FCSTD DOCUMENT  (FreeCAD 0.19R24291 (Git))
Label: battery-charger-assembly
License: All rights reserved
LicenseURL: http://en.wikipedia.org/wiki/All_rights_reserved
objects: App::Link×5, App::DocumentObjectGroup×2, PartDesign::CoordinateSystem×1, App::FeaturePython×1, App::Part×1
note: 1 computed .brp shape members not serialized (recipe doc carries the construction recipe); baked Part::Feature solids carry a one-line shape summary decoded from their .brp
EXTERNAL_REF file=battery-charger.FCStd obj=LCS_0
EXTERNAL_REF file=battery-charger.FCStd obj=battery_charger_part
EXTERNAL_REF file=micro-usb-b-connector.FCStd obj=LCS_0
EXTERNAL_REF file=micro-usb-b-connector.FCStd obj=micro_usb_b_part
EXTERNAL_REF file=usb-a-connector.FCStd obj=LCS_0
EXTERNAL_REF file=usb-a-connector.FCStd obj=usb_a_connector_part
EXTERNAL_REF file=slide_switch.FCStd obj=LCS_0
EXTERNAL_REF file=slide_switch.FCStd obj=switch_part
EXTERNAL_REF file=16340-battery.FCStd obj=LCS_0
EXTERNAL_REF file=16340-battery.FCStd obj=_6340_battery_part

FEATURE [App::DocumentObjectGroup] Parts
FEATURE [PartDesign::CoordinateSystem] LCS_Origin
  AttacherType = Attacher::AttachEngine3D
  MapMode = 2
  Support = -> [X_Axis]
FEATURE [App::DocumentObjectGroup] Constraints
FEATURE [App::FeaturePython] Variables  # WARN: FeaturePython — macro-defined, semantics opaque (R4)
FEATURE [App::Link] Unnamed_battery_charger_pcb_part  label="pcb"
  AssemblyType = Asm4EE
  AttachedBy = #LCS_0
  AttachedTo = Parent Assembly#LCS_Origin
  LinkedObject = -> <external battery-charger.FCStd>#battery_charger_part
  expr: Placement = LCS_Origin.Placement * AttachmentOffset * Unnamed#LCS_0.Placement ^ -1
FEATURE [App::Link] micro_usb
  AssemblyType = Asm4EE
  AttachedBy = #LCS_0
  AttachedTo = Unnamed_battery_charger_pcb_part#LCS_0
  AttachmentOffset = pos=(0,-27,1) rot=(0,0,1;1.5708rad)
  LinkPlacement = pos=(0,-27,1) rot=(0,0,1;1.5708rad)
  LinkedObject = -> <external micro-usb-b-connector.FCStd>#micro_usb_b_part
  Placement = pos=(0,-27,1) rot=(0,0,1;1.5708rad)
  expr: Placement = Unnamed_battery_charger_pcb_part.Placement * Unnamed#LCS_0.Placement * AttachmentOffset * Unnamed1#LCS_0.Placement ^ -1
FEATURE [App::Link] usb_a
  AssemblyType = Asm4EE
  AttachedBy = #LCS_0
  AttachedTo = Unnamed_battery_charger_pcb_part#LCS_0
  AttachmentOffset = pos=(0,30,0) rot=(0,0,1;0rad)
  LinkPlacement = pos=(0,30,0) rot=(0,0,1;0rad)
  LinkedObject = -> <external usb-a-connector.FCStd>#usb_a_connector_part
  Placement = pos=(0,30,0) rot=(0,0,1;0rad)
  expr: Placement = Unnamed_battery_charger_pcb_part.Placement * Unnamed#LCS_0.Placement * AttachmentOffset * Unnamed3#LCS_0.Placement ^ -1
FEATURE [App::Link] on_off_switch
  AssemblyType = Asm4EE
  AttachedBy = #LCS_0
  AttachedTo = Unnamed_battery_charger_pcb_part#LCS_0
  AttachmentOffset = pos=(11,19.5,0) rot=(0,0,1;1.5708rad)
  LinkPlacement = pos=(11,19.5,0) rot=(0,0,1;1.5708rad)
  LinkedObject = -> <external slide_switch.FCStd>#switch_part
  Placement = pos=(11,19.5,0) rot=(0,0,1;1.5708rad)
  expr: Placement = Unnamed_battery_charger_pcb_part.Placement * Unnamed#LCS_0.Placement * AttachmentOffset * Unnamed4#LCS_0.Placement ^ -1
FEATURE [App::Link] battery
  AssemblyType = Asm4EE
  AttachedBy = #LCS_0
  AttachedTo = Unnamed_battery_charger_pcb_part#LCS_0
  AttachmentOffset = pos=(0,-22,10) rot=(1,0,0;4.71239rad)
  LinkPlacement = pos=(0,-22,10) rot=(1,0,0;4.71239rad)
  LinkedObject = -> <external 16340-battery.FCStd>#_6340_battery_part
  Placement = pos=(0,-22,10) rot=(1,0,0;4.71239rad)
  expr: Placement = Unnamed_battery_charger_pcb_part.Placement * Unnamed#LCS_0.Placement * AttachmentOffset * Unnamed5#LCS_0.Placement ^ -1
FEATURE [App::Part] Model  label="battery_charger_assembly"
  Configuration = 0
  Group = -> [LCS_Origin,Constraints,Variables,Unnamed_battery_charger_pcb_part,micro_usb,usb_a,on_off_switch,battery]
  Origin = -> Origin
  Type = Assembly4 Model

RESOLVED EXTERNAL PARTS (link-assembly join: the EXTERNAL_REF files above that resolve inside this repo's crawl, each included once):
---- part 16340-battery.FCStd = doc fcstd_aa624853e9e1 ----
FCSTD DOCUMENT  (FreeCAD 0.19R24291 (Git))
Label: 16340-battery
License: All rights reserved
LicenseURL: http://en.wikipedia.org/wiki/All_rights_reserved
objects: PartDesign::AdditiveCylinder×2, PartDesign::CoordinateSystem×1, PartDesign::Body×1, App::Part×1
note: 6 computed .brp shape members not serialized (recipe doc carries the construction recipe); baked Part::Feature solids carry a one-line shape summary decoded from their .brp

FEATURE [PartDesign::CoordinateSystem] LCS_0
  AttacherType = Attacher::AttachEngine3D
  MapMode = 2
  Support = -> [X_Axis]
FEATURE [PartDesign::AdditiveCylinder] Cylinder  label="battery_cyl"
  Angle = 360
  AttacherType = Attacher::AttachEngine3D
  Height = 34
  MapMode = 5
  Radius = 8
  Support = -> [XY_Plane001]
FEATURE [PartDesign::AdditiveCylinder] Cylinder001  label="plus_cyl"
  Angle = 360
  AttacherType = Attacher::AttachEngine3D
  AttachmentOffset = pos=(0,0,34) rot=(0,0,1;0rad)
  BaseFeature = -> Cylinder
  Height = 1.5
  MapMode = 5
  Placement = pos=(0,0,34) rot=(0,0,1;0rad)
  Radius = 3
  Support = -> [XY_Plane001]
  expr: .AttachmentOffset.Base.z = <<battery_cyl>>.Height
FEATURE [PartDesign::Body] Body  label="battery_body"
  Group = -> [Cylinder,Cylinder001]
  Origin = -> Origin001
  Tip = -> Cylinder001
FEATURE [App::Part] _6340_battery_part  label="16340_battery_part"
  Group = -> [LCS_0,Body]
  Origin = -> Origin
---- part battery-charger.FCStd = doc fcstd_5544a6e2c195 ----
FCSTD DOCUMENT  (FreeCAD 0.19R24291 (Git))
Label: battery-charger
License: All rights reserved
LicenseURL: http://en.wikipedia.org/wiki/All_rights_reserved
objects: Sketcher::SketchObject×2, PartDesign::CoordinateSystem×1, PartDesign::Pad×1, PartDesign::Pocket×1, PartDesign::Body×1, App::Part×1
note: 8 computed .brp shape members not serialized (recipe doc carries the construction recipe); baked Part::Feature solids carry a one-line shape summary decoded from their .brp

FEATURE [PartDesign::CoordinateSystem] LCS_0
  AttacherType = Attacher::AttachEngine3D
  MapMode = 2
  Support = -> [X_Axis]
FEATURE [Sketcher::SketchObject] Sketch  label="sk_pcb"
  FullyConstrained = true
  MapMode = 5
  Support = -> [XY_Plane001]
  sketch-geometry (12):
    g0: LineSegment StartX=-12.5 StartY=30 StartZ=0 EndX=12.5 EndY=30 EndZ=0
    g1: LineSegment StartX=14 StartY=28.5 StartZ=0 EndX=14 EndY=-28.5 EndZ=0
    g2: LineSegment StartX=12.5 StartY=-30 StartZ=0 EndX=-12.5 EndY=-30 EndZ=0
    g3: LineSegment StartX=-14 StartY=-28.5 StartZ=0 EndX=-14 EndY=28.5 EndZ=0
    g4: Circle CenterX=-12 CenterY=28 CenterZ=0 NormalX=0 NormalY=0 NormalZ=1 AngleXU=0 Radius=1.5
    g5: Circle CenterX=12 CenterY=28 CenterZ=0 NormalX=0 NormalY=0 NormalZ=1 AngleXU=0 Radius=1.5
    g6: Circle CenterX=-12 CenterY=-28 CenterZ=0 NormalX=0 NormalY=0 NormalZ=1 AngleXU=0 Radius=1.5
    g7: Circle CenterX=12 CenterY=-28 CenterZ=0 NormalX=0 NormalY=0 NormalZ=1 AngleXU=0 Radius=1.5
    g8: ArcOfCircle CenterX=-12.5 CenterY=28.5 CenterZ=0 NormalX=0 NormalY=0 NormalZ=1 AngleXU=0 Radius=1.5 StartAngle=1.5708 EndAngle=3.14159
    g9: ArcOfCircle CenterX=12.5 CenterY=28.5 CenterZ=0 NormalX=0 NormalY=0 NormalZ=1 AngleXU=0 Radius=1.5 StartAngle=-9e-16 EndAngle=1.5708
    g10: ArcOfCircle CenterX=12.5 CenterY=-28.5 CenterZ=0 NormalX=0 NormalY=0 NormalZ=1 AngleXU=0 Radius=1.5 StartAngle=4.71239 EndAngle=6.28319
    g11: ArcOfCircle CenterX=-12.5 CenterY=-28.5 CenterZ=0 NormalX=0 NormalY=0 NormalZ=1 AngleXU=0 Radius=1.5 StartAngle=3.14159 EndAngle=4.71239
  constraints (28):
    c: Horizontal(g2)
    c: Vertical(g1)
    c: Diameter(g6) = 3  'hole_diameter'
    c: Equal(g6,g7)
    c: Equal(g6,g5)
    c: Equal(g6,g4)
    c: Symmetric(g5,g4,g-2)
    c: Symmetric(g6,g7,g-2)
    c: Symmetric(g6,g4,g-1)
    c: Tangent(g0,g8) = 1.5708
    c: Tangent(g3,g8) = 1.5708
    c: Tangent(g0,g9) = 1.5708
    c: Tangent(g1,g9) = 1.5708
    c: Tangent(g1,g10) = 1.5708
    c: Tangent(g2,g10) = 1.5708
    c: Tangent(g2,g11) = 1.5708
    c: Tangent(g3,g11) = 1.5708
    c: Vertical(g3)
    c: Symmetric(g10,g11,g-2)
    c: DistanceY(g2,g0) = 60  'length'
    c: DistanceX(g3,g1) = 28  'width'
    c: DistanceX(g3,g4) = 2
    c: DistanceY(g4,g0) = 2
    c: Horizontal(g0)
    c: Equal(g8,g9)
    c: Equal(g9,g10)
    c: DistanceY(g2,g7) = 2
    c: Equal(g5,g9)
FEATURE [PartDesign::Pad] Pad  label="pad_pcb"
  Direction = (1,1,1)
  Length = 1
  Length2 = 100
  Profile = -> Sketch
  Type = 0
FEATURE [Sketcher::SketchObject] Sketch001  label="sk_pin_holes"
  FullyConstrained = true
  MapMode = 5
  Support = -> [XY_Plane001]
  expr: Constraints[23] = <<sk_pcb>>.Constraints.width / 2 - 1mm - .Constraints.pin_hole_diameter / 2
  expr: Constraints[22] = <<sk_pcb>>.Constraints.length / 2 - 10mm - .Constraints.pin_hole_diameter / 2
  expr: Constraints[19] = .Constraints.pin_spacing
  expr: Constraints[17] = .Constraints.pin_spacing
  expr: Constraints[18] = .Constraints.pin_spacing
  expr: Constraints[16] = .Constraints.pin_spacing
  sketch-geometry (10):
    g0: Circle CenterX=-12.5 CenterY=19.5 CenterZ=0 NormalX=0 NormalY=0 NormalZ=1 AngleXU=0 Radius=0.5
    g1: Circle CenterX=-12.5 CenterY=17 CenterZ=0 NormalX=0 NormalY=0 NormalZ=1 AngleXU=0 Radius=0.5
    g2: Circle CenterX=-12.5 CenterY=1.25 CenterZ=0 NormalX=0 NormalY=0 NormalZ=1 AngleXU=0 Radius=0.5
    g3: Circle CenterX=-12.5 CenterY=-1.25 CenterZ=0 NormalX=0 NormalY=0 NormalZ=1 AngleXU=0 Radius=0.5
    g4: Circle CenterX=-12.5 CenterY=-17 CenterZ=0 NormalX=0 NormalY=0 NormalZ=1 AngleXU=0 Radius=0.5
    g5: Circle CenterX=-12.5 CenterY=-19.5 CenterZ=0 NormalX=0 NormalY=0 NormalZ=1 AngleXU=0 Radius=0.5
    g6: Circle CenterX=12.5 CenterY=-17 CenterZ=0 NormalX=0 NormalY=0 NormalZ=1 AngleXU=0 Radius=0.5
    g7: Circle CenterX=12.5 CenterY=-19.5 CenterZ=0 NormalX=0 NormalY=0 NormalZ=1 AngleXU=0 Radius=0.5
    g8: Circle CenterX=12.5 CenterY=1.25 CenterZ=0 NormalX=0 NormalY=0 NormalZ=1 AngleXU=0 Radius=0.5
    g9: Circle CenterX=12.5 CenterY=-1.25 CenterZ=0 NormalX=0 NormalY=0 NormalZ=1 AngleXU=0 Radius=0.5
  constraints (22):
    c: Diameter(g0) = 1  'pin_hole_diameter'
    c: Equal(g0, g1-g5) x5
    c: Equal(g0,g7)
    c: Equal(g0,g6)
    c: Equal(g0,g9)
    c: Equal(g0,g8)
    c: Vertical(g0,g1)
    c: Vertical(g1,g2)
    c: Vertical(g4,g5)
    c: Vertical(g8,g9)
    c: Vertical(g6,g7)
    c: DistanceY(g1,g0) = 2.5  'pin_spacing'
    c: DistanceY(g3,g2) = 2.5
    c: DistanceY(g9,g8) = 2.5
    c: DistanceY(g5,g4) = 2.5
    c: DistanceY(g7,g6) = 2.5
    c: Symmetric(g2,g8,g-2)
    c: Symmetric(g6,g4,g-2)
    c: DistanceY(g-1,g0) = 19.5
    c: DistanceX(g1,g-1) = 12.5
    c: Symmetric(g2,g3,g-1)
    c: Symmetric(g1,g4,g-1)
FEATURE [PartDesign::Pocket] Pocket
  BaseFeature = -> Pad
  Length = 5
  Length2 = 100
  Profile = -> Sketch001
  Reversed = true
  Type = 1
FEATURE [PartDesign::Body] Body  label="battery_charger_body"
  Group = -> [Sketch,Pad,Sketch001,Pocket]
  Origin = -> Origin001
  Tip = -> Pocket
FEATURE [App::Part] battery_charger_part  label="battery_charger_pcb_part"
  Group = -> [LCS_0,Body]
  Origin = -> Origin
---- part micro-usb-b-connector.FCStd = doc fcstd_086b0453c2a9 (86199 chars; too large to inline — full recipe in that document) ----
